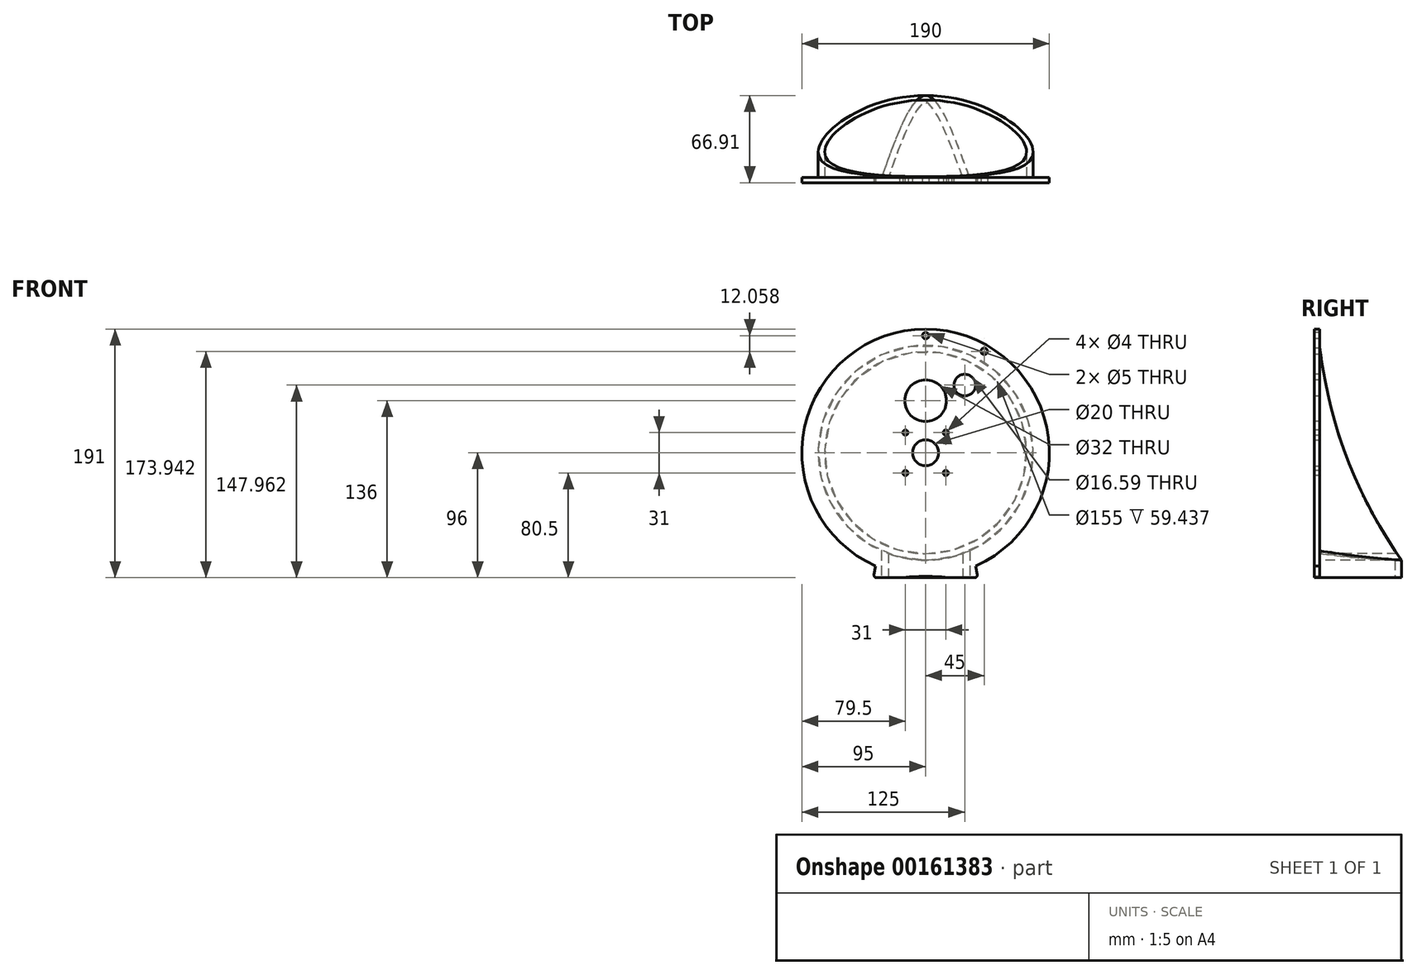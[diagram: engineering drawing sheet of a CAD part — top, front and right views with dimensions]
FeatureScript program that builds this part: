
annotation { "Feature Type Name" : "Feature", "Feature Type Description" : "" }
export const myFeature = defineFeature(function(context is Context, id is Id, definition is map)
    precondition{}
    {
        {
            var Q0;
            Q0=qCreatedBy(makeId("Front.planeOp"),FACE);
            var sketch = newSketch(context, id + "F0", { "sketchPlane" : qUnion([Q0])});
            skCircle(sketch, "E0", {"center": v(0, 0) * mm, "radius": 95 * mm});
            skCircle(sketch, "E1", {"center": v(0, 0) * mm, "radius": 10 * mm});
            skSolve(sketch);
        }
        {
            var Q0;
            Q0 = qSketchRegion(id + "F0", true);
            extrude(context, id + "F1", {"entities" : qUnion([Q0]), "depth" : 4 * mm});
        }
        {
            var Q0;
            Q0=makeQuery(id+"F1.opExtrude","CAP_FACE",FACE,{"disambiguationData":[OSD([sQuery(id+"F0.wireOp",EDGE,"E0"),sQuery(id+"F0.wireOp",EDGE,"E1")])],"isStart":false});
            var sketch = newSketch(context, id + "F2", { "sketchPlane" : qUnion([Q0])});
            skLineSegment(sketch, "E2", {"start": v(0, 0) * mm, "end": v(0, 40) * mm, "construction": true});
            skCircle(sketch, "E3", {"center": v(0, 40) * mm, "radius": 16 * mm});
            skLineSegment(sketch, "E4", {"start": v(0, 0) * mm, "end": v(30, 51.96) * mm, "construction": true});
            skLineSegment(sketch, "E5", {"start": v(13.86, 32) * mm, "end": v(-0.86, 6.5) * mm, "construction": true});
            skCircle(sketch, "E6", {"center": v(30, 51.96) * mm, "radius": 8.3 * mm});
            skCircle(sketch, "E7", {"center": v(0, 90) * mm, "radius": 2.5 * mm});
            skCircle(sketch, "E8", {"center": v(45, 77.94) * mm, "radius": 2.5 * mm});
            skCircle(sketch, "E9", {"center": v(0, 0) * mm, "radius": 90 * mm, "construction": true});
            skSolve(sketch);
        }
        {
            var Q0;
            Q0 = qSketchRegion(id + "F2", true);
            extrude(context, id + "F3", {"entities" : qUnion([Q0]), "operationType" : NewBodyOperationType.REMOVE, "endBound" : BoundingType.THROUGH_ALL, "oppositeDirection" : true, "depth" : 25 * mm});
        }
        {
            var Q0;
            Q0=makeQuery(id+"F1.opExtrude","CAP_FACE",FACE,{"disambiguationData":[OSD([sQuery(id+"F0.wireOp",EDGE,"E0"),sQuery(id+"F0.wireOp",EDGE,"E1")])],"isStart":false});
            var sketch = newSketch(context, id + "F4", { "sketchPlane" : qUnion([Q0])});
            skLineSegment(sketch, "E10", {"start": v(0, 0) * mm, "end": v(0, -116.75) * mm, "construction": true});
            skLineSegment(sketch, "E11", {"start": v(-38.4, -86.9) * mm, "end": v(-40, -96) * mm});
            skLineSegment(sketch, "E12", {"start": v(-40, -96) * mm, "end": v(-20, -96) * mm});
            skArc(sketch, "E13", {"start": v(0, -95) * mm, "mid": v(-10.01, -95.25) * mm, "end": v(-20, -96) * mm});
            skLineSegment(sketch, "E14.MirrorCS", {"start": v(38.4, -86.9) * mm, "end": v(40, -96) * mm});
            skLineSegment(sketch, "E15.MirrorCS", {"start": v(40, -96) * mm, "end": v(20, -96) * mm});
            skArc(sketch, "E16.MirrorCS", {"start": v(0, -95) * mm, "mid": v(10.01, -95.25) * mm, "end": v(20, -96) * mm});
            skArc(sketch, "E17.0", {"start": v(-38.4, -86.9) * mm, "mid": v(0, -95) * mm, "end": v(38.4, -86.9) * mm});
            skSolve(sketch);
        }
        {
            var Q0;
            Q0 = qSketchRegion(id + "F4", true);
            var Q1;
            Q1=makeQuery(id+"F1.opExtrude","CAP_FACE",FACE,{"disambiguationData":[OSD([sQuery(id+"F0.wireOp",EDGE,"E0"),sQuery(id+"F0.wireOp",EDGE,"E1")])],"isStart":true});
            extrude(context, id + "F5", {"entities" : qUnion([Q0]), "operationType" : NewBodyOperationType.ADD, "endBound" : BoundingType.UP_TO_SURFACE, "oppositeDirection" : true, "endBoundEntityFace" : qUnion([Q1]), "depth" : 25 * mm});
        }
        {
            var Q0;
            Q0=makeQuery(id+"F5.opExtrude","SWEPT_EDGE",EDGE,{"disambiguationData":[OSD([sQuery(id+"F0.wireOp",EDGE,"E0"),sQuery(id+"F4.wireOp",EDGE,"E11"),sQuery(id+"F4.wireOp",EDGE,"E17.0")])]});
            var Q1;
            Q1=makeQuery(id+"F5.opExtrude","SWEPT_EDGE",EDGE,{"disambiguationData":[OSD([sQuery(id+"F0.wireOp",EDGE,"E0"),sQuery(id+"F4.wireOp",EDGE,"E14.MirrorCS"),sQuery(id+"F4.wireOp",EDGE,"E17.0")])]});
            var Q2;
            Q2=makeQuery(id+"F5.opExtrude","SWEPT_EDGE",EDGE,{"disambiguationData":[OSD([sQuery(id+"F4.wireOp",EDGE,"E14.MirrorCS"),sQuery(id+"F4.wireOp",EDGE,"E15.MirrorCS")])]});
            var Q3;
            Q3=makeQuery(id+"F5.opExtrude","SWEPT_EDGE",EDGE,{"disambiguationData":[OSD([sQuery(id+"F4.wireOp",EDGE,"E11"),sQuery(id+"F4.wireOp",EDGE,"E12")])]});
            fillet(context, id + "F6", {"entities" : qUnion([Q0, Q1, Q2, Q3]), "radius" : 2 * mm, "tangentPropagation" : true, "allowEdgeOverflow" : false});
        }
        {
            var Q0;
            {var subQ0=sQuery(id+"F4.wireOp",EDGE,"E17.0");Q0=makeQuery(id+"F5.boolean.opBoolean","MERGE",FACE,{"derivedFrom":[makeQuery(id+"F1.opExtrude","CAP_FACE",FACE,{"disambiguationData":[OSD([sQuery(id+"F0.wireOp",EDGE,"E0"),sQuery(id+"F0.wireOp",EDGE,"E1")])],"isStart":false}),makeQuery(id+"F5.opExtrude","CAP_FACE",FACE,{"disambiguationData":[OSD([sQuery(id+"F4.wireOp",EDGE,"E11"),sQuery(id+"F4.wireOp",EDGE,"E12"),sQuery(id+"F4.wireOp",EDGE,"E13"),subQ0])],"isStart":true}),makeQuery(id+"F5.opExtrude","CAP_FACE",FACE,{"disambiguationData":[OSD([sQuery(id+"F4.wireOp",EDGE,"E14.MirrorCS"),sQuery(id+"F4.wireOp",EDGE,"E15.MirrorCS"),sQuery(id+"F4.wireOp",EDGE,"E16.MirrorCS"),subQ0])],"isStart":true})]});}
            var sketch = newSketch(context, id + "F7", { "sketchPlane" : qUnion([Q0])});
            skLineSegment(sketch, "E18.bottom", {"start": v(15.5, 15.5) * mm, "end": v(-15.5, 15.5) * mm, "construction": true});
            skLineSegment(sketch, "E18.top", {"start": v(15.5, -15.5) * mm, "end": v(-15.5, -15.5) * mm, "construction": true});
            skLineSegment(sketch, "E18.left", {"start": v(15.5, 15.5) * mm, "end": v(15.5, -15.5) * mm, "construction": true});
            skLineSegment(sketch, "E18.right", {"start": v(-15.5, 15.5) * mm, "end": v(-15.5, -15.5) * mm, "construction": true});
            skPoint(sketch, "E18.middle", {"position": v(0, 0) * mm});
            skCircle(sketch, "E19", {"center": v(-15.5, 15.5) * mm, "radius": 2 * mm});
            skCircle(sketch, "E20", {"center": v(15.5, -15.5) * mm, "radius": 2 * mm});
            skCircle(sketch, "E21", {"center": v(15.5, 15.5) * mm, "radius": 2 * mm});
            skCircle(sketch, "E22", {"center": v(-15.5, -15.5) * mm, "radius": 2 * mm});
            skSolve(sketch);
        }
        {
            var Q0;
            Q0 = qSketchRegion(id + "F7", true);
            extrude(context, id + "F8", {"entities" : qUnion([Q0]), "operationType" : NewBodyOperationType.REMOVE, "endBound" : BoundingType.THROUGH_ALL, "oppositeDirection" : true, "depth" : 25 * mm});
        }
        {
            var Q0;
            {var subQ0=sQuery(id+"F4.wireOp",EDGE,"E17.0");Q0=makeQuery(id+"F5.boolean.opBoolean","MERGE",FACE,{"derivedFrom":[makeQuery(id+"F1.opExtrude","CAP_FACE",FACE,{"disambiguationData":[OSD([sQuery(id+"F0.wireOp",EDGE,"E0"),sQuery(id+"F0.wireOp",EDGE,"E1")])],"isStart":true}),makeQuery(id+"F5.opExtrude","CAP_FACE",FACE,{"disambiguationData":[OSD([sQuery(id+"F4.wireOp",EDGE,"E11"),sQuery(id+"F4.wireOp",EDGE,"E12"),sQuery(id+"F4.wireOp",EDGE,"E13"),subQ0])],"isStart":false}),makeQuery(id+"F5.opExtrude","CAP_FACE",FACE,{"disambiguationData":[OSD([sQuery(id+"F4.wireOp",EDGE,"E14.MirrorCS"),sQuery(id+"F4.wireOp",EDGE,"E15.MirrorCS"),sQuery(id+"F4.wireOp",EDGE,"E16.MirrorCS"),subQ0])],"isStart":false})]});}
            var sketch = newSketch(context, id + "F9", { "sketchPlane" : qUnion([Q0])});
            skCircle(sketch, "E23", {"center": v(0, 0) * mm, "radius": 82.5 * mm});
            skCircle(sketch, "E24", {"center": v(0, 0) * mm, "radius": 77.5 * mm});
            skSolve(sketch);
        }
        {
            var Q0;
            Q0=qCreatedBy(makeId("Right.planeOp"),FACE);
            var sketch = newSketch(context, id + "F10", { "sketchPlane" : qUnion([Q0])});
            skArc(sketch, "E25", {"start": v(0, 83) * mm, "mid": v(27.04, -18.73) * mm, "end": v(82.79, -108.04) * mm});
            skSolve(sketch);
        }
        {
            var Q0;
            Q0 = qSketchRegion(id + "F10", true);
            var Q1;
            Q1=sQuery(id+"F10.wireOp",EDGE,"E25");
            extrude(context, id + "F11", {"entities" : qUnion([Q0]), "bodyType" : ToolBodyType.SURFACE, "surfaceEntities" : qUnion([Q1]), "endBound" : BoundingType.SYMMETRIC, "depth" : 200 * mm});
        }
        {
            var Q0;
            Q0=makeQuery(id+"F9.imprint","IMPRINT",FACE,{"disambiguationData":[TD([[makeQuery(id+"F9.imprint","IMPRINT",EDGE,{"derivedFrom":sQuery(id+"F9.wireOp",EDGE,"E23")}),1.0]])]});
            var Q1;
            Q1=makeQuery(id+"F11.opExtrude","SWEPT_BODY",BODY,{"disambiguationData":[OSD([sQuery(id+"F10.wireOp",EDGE,"E25")])]});
            extrude(context, id + "F12", {"entities" : qUnion([Q0]), "operationType" : NewBodyOperationType.ADD, "endBound" : BoundingType.UP_TO_BODY, "endBoundEntityBody" : qUnion([Q1]), "depth" : 25 * mm});
        }
        {
            var Q0;
            Q0=makeQuery(id+"F5.opExtrude","SWEPT_FACE",FACE,{"disambiguationData":[OSD([sQuery(id+"F4.wireOp",EDGE,"E15.MirrorCS")])]});
            var sketch = newSketch(context, id + "F13", { "sketchPlane" : qUnion([Q0])});
            skLineSegment(sketch, "E26", {"start": v(0, 0) * mm, "end": v(0, -87.37) * mm, "construction": true});
            skFitSpline(sketch, "E27", {"points": [v(33.86, 0) * mm, v(0, -62.91) * mm, v(-33.86, 0) * mm], "startDerivative": vector(-70.9, -190.4) * mm, "endDerivative": vector(-67.26, 190.69) * mm});
            skFitSpline(sketch, "E28.0", {"points": [v(29.17, 1.74) * mm, v(27.7, -2.23) * mm, v(24.77, -10.14) * mm, v(20.47, -21.55) * mm, v(16.27, -32.12) * mm, v(12.84, -39.92) * mm, v(10.15, -45.34) * mm, v(8.18, -48.94) * mm, v(6.26, -52.01) * mm, v(4.43, -54.5) * mm, v(2.76, -56.33) * mm, v(1.59, -57.26) * mm, v(0.87, -57.67) * mm, v(0.46, -57.83) * mm, v(0.23, -57.9) * mm, v(0.08, -57.9) * mm, v(0, -57.91) * mm, v(-0.1, -57.9) * mm, v(-0.24, -57.9) * mm, v(-0.48, -57.83) * mm, v(-0.9, -57.66) * mm, v(-1.64, -57.25) * mm, v(-2.84, -56.3) * mm, v(-4.55, -54.48) * mm, v(-6.4, -52) * mm, v(-8.36, -48.92) * mm, v(-10.36, -45.33) * mm, v(-13.09, -39.92) * mm, v(-16.55, -32.14) * mm, v(-20.74, -21.6) * mm, v(-24.94, -10.2) * mm, v(-27.74, -2.3) * mm, v(-29.14, 1.66) * mm]});
            skLineSegment(sketch, "E29", {"start": v(33.86, 0) * mm, "end": v(29.17, 1.74) * mm});
            skLineSegment(sketch, "E30", {"start": v(-33.86, 0) * mm, "end": v(-29.14, 1.66) * mm});
            skSolve(sketch);
        }
        {
            var Q0;
            Q0 = qSketchRegion(id + "F13", true);
            var Q1;
            Q1=makeQuery(id+"F12.opExtrude","SWEPT_FACE",FACE,{"disambiguationData":[OSD([sQuery(id+"F9.wireOp",EDGE,"E23")])]});
            extrude(context, id + "F14", {"entities" : qUnion([Q0]), "operationType" : NewBodyOperationType.ADD, "endBound" : BoundingType.UP_TO_SURFACE, "oppositeDirection" : true, "endBoundEntityFace" : qUnion([Q1]), "depth" : 25 * mm});
        }
    });
